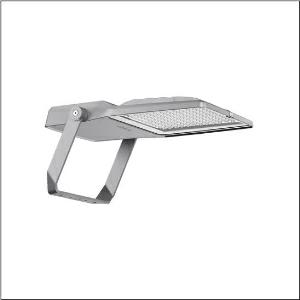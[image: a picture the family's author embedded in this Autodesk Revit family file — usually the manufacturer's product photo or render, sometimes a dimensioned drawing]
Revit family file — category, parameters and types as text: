
# Revit family: floodlight_fl_21_iq_midi___rs12_5xa7781e6b1a_09af
name_source: partatom
category: Lighting Fixtures
units: mm (PartAtom-declared; Revit-internal decimal feet)

## family parameters
Cut with Voids When Loaded = No
Host = Face
Light Source = No
Part Type = Normal
Room Calculation Point = No
Round Connector Dimension = Use Diameter
Shared = No

## types (1)
- --- (1 x LED, 21420 lm, 208.1 W, 5700K)
    Apparent Load = 208 VA
    CIE Flux Codes = 79 92 99 100 100
    Color Rendering = 90
    Color Temperature = 5700K
    Default Elevation = 1800 mm
    Description = Floodlight FL 21 iQ midi, floodlight, primary light control with lens, of PMMA, primary optical cover: protective disc, of toughened safety glass, transparent, light distribution: RS12, light emission: direct distribution, installation type: surface-mounted, LED, High Power LED, rated luminous flux: 21.420lm, luminous efficacy: 103lm/W, light colour: 957, colour temperature: 5700K, control gear: ECG iQ, control: optimised constant luminous flux control (CLO 2.0), Desk-Remote (wireless, voltage-free reading and setting of iQ features in the workshop via application-optimized NFC function/RFID function), Light-Fading, Smart-Wire, Night-Set, Lumen-Switch, Temp-Guard, Auto-Match, with terminal, 6-pole, mains connection: 220..240V, AC, 50/60Hz, start of lifetime: 208W, end of service life: 227W, reduction: 90W, luminaire housing, of diecast aluminium, powder-coated, Siteco® metallic grey (DB 702S), corrosivity category C5 mid according to DIN EN ISO 12944, sealing non-destructively replaceable, mounting bracket, of steel, galvanised, powder-coated, Siteco® metallic grey (DB 702S), protection rating (complete): IP66, insulation class (complete): insulation class II (safety insulation), certification: CE, protection symbol: D, impact resistance: IK08, permissible operating ambient temperature: -40..+40°C, permissible operating ambient temperature for outdoor applications: -40..+50°C, standard: DIN EN 12944, LABS conformity tested according to VDMA 24364:2018-05, packaging unit: 1 piece

Light Distribution: RS12
    Height = 76 mm
    Lamp = 1 x LED
    Lamp Light Flux = 21420 lm
    Lamp Power = 208.1 W
    Lamp count = 1
    Length = 657 mm
    Luminous efficacy = 103 lm/W
    Manufacturer = Siteco
    ModVariant = No
    Model = 5XA7781E6B1A
    Number of Poles = 1
    OnlyDefault = Yes
    Power Factor = 1
    Product Name = Floodlight FL 21 iQ midi | RS12
    Product group = floodlight | pylon annexe
    ProductGroupID = 6200
    Protection Class = Protection class II
    Protection Degree = IP 66
    RLX_Detail_Level = 1
    RLX_Emergency_Light_Flux = 0 lm
    RLX_Emergency_Type = 0
    RLX_Emergency_Type_DB = No
    RlxData = <blob elided: 141109 chars, md5=cb97d3e0>
    Socket = socket
    Standby Power = 0 W
    System Light Flux = 21420 lm
    System Power = 208 W
    Type Comments = factory setting: luminous flux: 100 % | dim-lin: 254 | 710 mA
    Type Image = l_1006876.jpg
    URL = http://relux.com
    VarID = @adj_055951
    Voltage = 0 V
    Weight = 0.00 kg
    Width = 442 mm

## geometry (parser evidence)
native form markers: Blend x4, Sweep x11
no freeform markers — native parametric forms only
